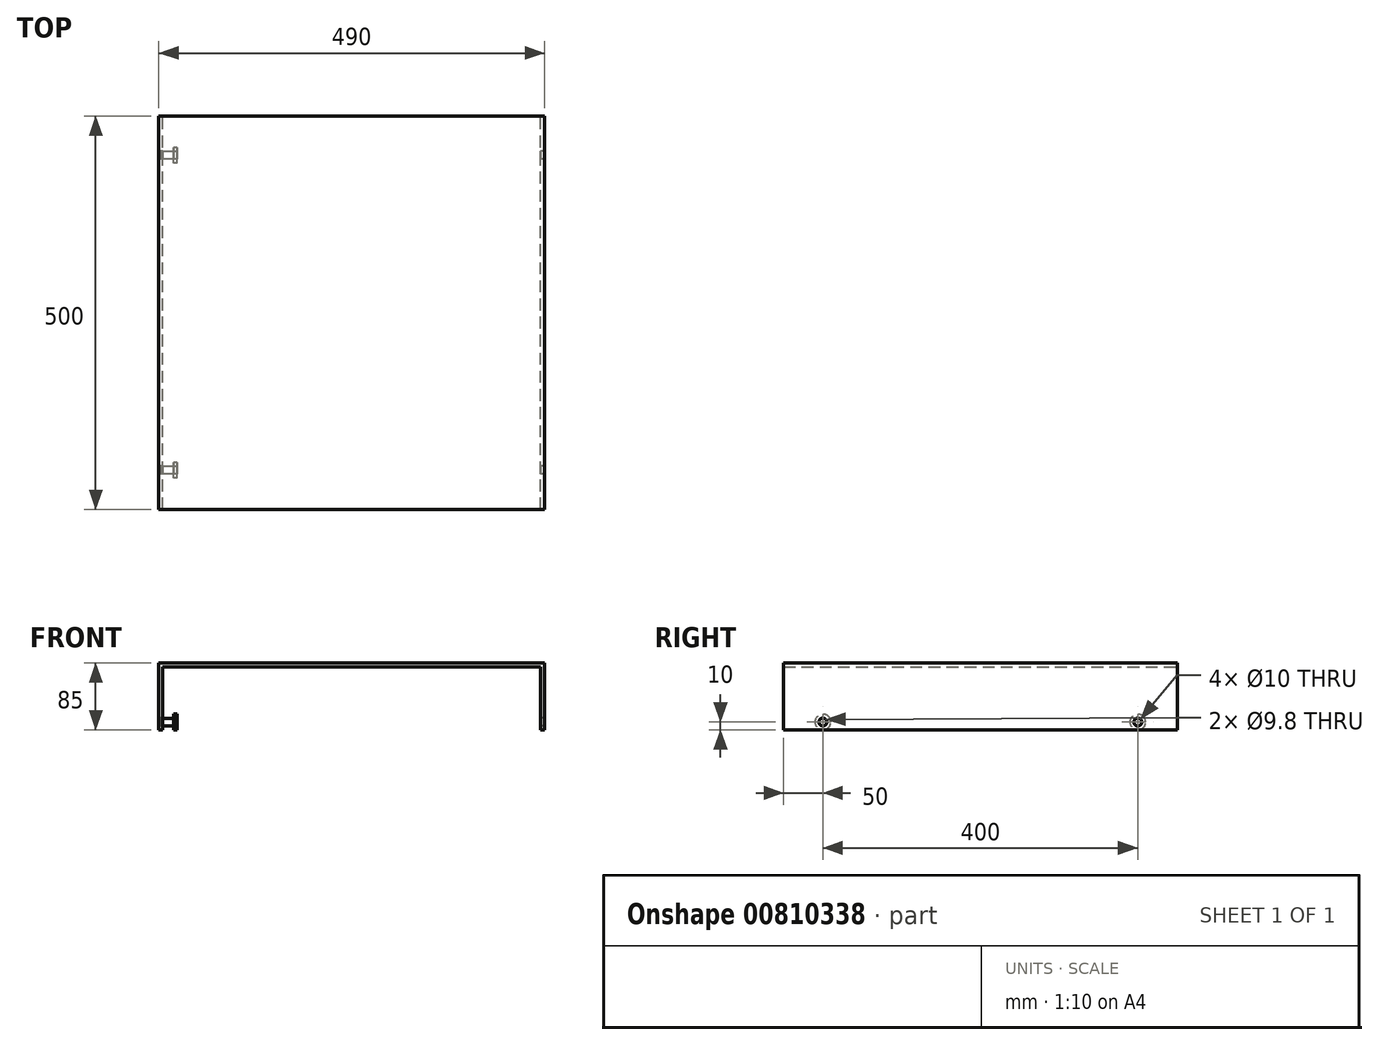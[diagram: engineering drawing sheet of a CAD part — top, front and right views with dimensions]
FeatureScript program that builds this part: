
annotation { "Feature Type Name" : "Feature", "Feature Type Description" : "" }
export const myFeature = defineFeature(function(context is Context, id is Id, definition is map)
    precondition{}
    {
        {
            var Q0;
            Q0=qCreatedBy(makeId("Front.planeOp"),FACE);
            var sketch = newSketch(context, id + "F0", { "sketchPlane" : qUnion([Q0])});
            skLineSegment(sketch, "E0", {"start": v(-245, 85) * mm, "end": v(-245, 170) * mm});
            skLineSegment(sketch, "E1", {"start": v(-245, 170) * mm, "end": v(245, 170) * mm});
            skLineSegment(sketch, "E2", {"start": v(245, 170) * mm, "end": v(245, 85) * mm});
            skLineSegment(sketch, "E3", {"start": v(0, 405.6) * mm, "end": v(0, -302.53) * mm, "construction": true});
            skLineSegment(sketch, "E4", {"start": v(-384.6, 0) * mm, "end": v(428.5, 0) * mm, "construction": true});
            skLineSegment(sketch, "E5.0", {"start": v(240, 165) * mm, "end": v(240, 85) * mm});
            skLineSegment(sketch, "E5.1", {"start": v(-240, 165) * mm, "end": v(240, 165) * mm});
            skLineSegment(sketch, "E5.2", {"start": v(-240, 85) * mm, "end": v(-240, 165) * mm});
            skLineSegment(sketch, "E6", {"start": v(-245, 85) * mm, "end": v(-240, 85) * mm});
            skLineSegment(sketch, "E7", {"start": v(240, 85) * mm, "end": v(245, 85) * mm});
            skSolve(sketch);
        }
        {
            var Q0;
            Q0 = qSketchRegion(id + "F0", true);
            extrude(context, id + "F1", {"entities" : qUnion([Q0]), "depth" : 500 * mm, "offsetDistance" : 25.4 * mm});
        }
        {
            var Q0;
            Q0=makeQuery(id+"F1.opExtrude","SWEPT_FACE",FACE,{"disambiguationData":[OSD([sQuery(id+"F0.wireOp",EDGE,"E0")])]});
            var sketch = newSketch(context, id + "F2", { "sketchPlane" : qUnion([Q0])});
            skLineSegment(sketch, "E8", {"start": v(0, 95) * mm, "end": v(514.43, 95) * mm, "construction": true});
            skCircle(sketch, "E9", {"center": v(50, 95) * mm, "radius": 5 * mm});
            skCircle(sketch, "E10.1.0.0", {"center": v(450, 95) * mm, "radius": 5 * mm});
            skLineSegment(sketch, "E10.direction1", {"start": v(50, 95) * mm, "end": v(450, 95) * mm, "construction": true});
            skSolve(sketch);
        }
        {
            var Q0;
            Q0 = qSketchRegion(id + "F2", true);
            extrude(context, id + "F3", {"entities" : qUnion([Q0]), "operationType" : NewBodyOperationType.REMOVE, "endBound" : BoundingType.THROUGH_ALL, "oppositeDirection" : true, "depth" : 25.4 * mm, "offsetDistance" : 25.4 * mm});
        }
        {
            var Q0;
            Q0=makeQuery(id+"F1.opExtrude","SWEPT_FACE",FACE,{"disambiguationData":[OSD([sQuery(id+"F0.wireOp",EDGE,"E5.2")])]});
            var sketch = newSketch(context, id + "F4", { "sketchPlane" : qUnion([Q0])});
            skCircle(sketch, "E11", {"center": v(-450, 95) * mm, "radius": 4.9 * mm});
            skCircle(sketch, "E12", {"center": v(-50, 95) * mm, "radius": 4.9 * mm});
            skSolve(sketch);
        }
        {
            var Q0;
            Q0 = qSketchRegion(id + "F4", true);
            extrude(context, id + "F5", {"entities" : qUnion([Q0]), "operationType" : NewBodyOperationType.ADD, "depth" : 14 * mm, "offsetDistance" : 25.4 * mm, "hasSecondDirection" : true, "secondDirectionOppositeDirection" : true, "secondDirectionDepth" : 2.5 * mm});
        }
        {
            var Q0;
            Q0=makeQuery(id+"F5.opExtrude","CAP_FACE",FACE,{"disambiguationData":[OSD([sQuery(id+"F4.wireOp",EDGE,"E12")])],"isStart":false});
            var sketch = newSketch(context, id + "F6", { "sketchPlane" : qUnion([Q0])});
            skCircle(sketch, "E13", {"center": v(-50, 95) * mm, "radius": 10 * mm});
            skCircle(sketch, "E14", {"center": v(-50, 95) * mm, "radius": 4.9 * mm});
            skSolve(sketch);
        }
        {
            var Q0;
            Q0 = qSketchRegion(id + "F6", true);
            extrude(context, id + "F7", {"entities" : qUnion([Q0]), "operationType" : NewBodyOperationType.ADD, "depth" : 4 * mm, "offsetDistance" : 25.4 * mm});
        }
        {
            var Q0;
            Q0=makeQuery(id+"F5.opExtrude","CAP_FACE",FACE,{"disambiguationData":[OSD([sQuery(id+"F4.wireOp",EDGE,"E11")])],"isStart":false});
            var sketch = newSketch(context, id + "F8", { "sketchPlane" : qUnion([Q0])});
            skCircle(sketch, "E15", {"center": v(-450, 95) * mm, "radius": 10 * mm});
            skCircle(sketch, "E16", {"center": v(-450, 95) * mm, "radius": 4.9 * mm});
            skSolve(sketch);
        }
        {
            var Q0;
            Q0 = qSketchRegion(id + "F8", true);
            extrude(context, id + "F9", {"entities" : qUnion([Q0]), "operationType" : NewBodyOperationType.ADD, "depth" : 4 * mm, "offsetDistance" : 25.4 * mm});
        }
    });
